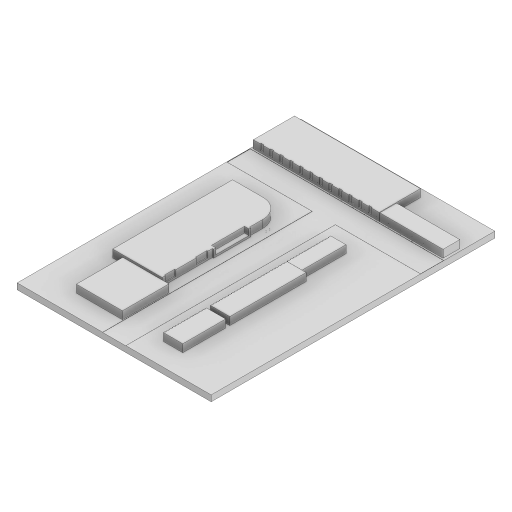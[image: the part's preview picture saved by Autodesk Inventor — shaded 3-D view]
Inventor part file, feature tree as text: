
AUTODESK INVENTOR PART (.ipt)
format: ipt  version: 2023 (Build 270158000, 158)  size: 555,008 bytes
history: native  units: in
note: dims shown in document units (in); Inventor stores cm internally (conversion verified against a paired STEP export)
features: projected_geometry x16, extrude x10, sketch x10, pattern_linear x3
ambient origin geometry x8: Origin, YZ Plane, XZ Plane, XY Plane, X Axis, Y Axis, Z Axis, Center Point
bodies: Solid1 (feature_tree)
feature tree (39):
  extrude  "Extrusion1"  Depth=472.4409in
  extrude  "Extrusion2"  Depth=3937.0079in
  extrude  "Extrusion3"  Depth=4.0in TaperAngle=0.0deg
  extrude  "Extrusion4"  Depth=157.4803in TaperAngle=0.0deg
  extrude  "Extrusion5"  Depth=118.1102in TaperAngle=0.0deg
  extrude  "Extrusion6"  Depth=118.1102in TaperAngle=0.0deg
  extrude  "Extrusion7"  Depth=39.3701in
  extrude  "Extrusion8"  Depth=78.7402in
  pattern_linear  "Rectangular Pattern1"  Count1=200 Spacing1=0.0in
  extrude  "Extrusion9"  Depth=118.1102in TaperAngle=0.0deg
  pattern_linear  "Rectangular Pattern2"  Count1=10 Spacing1=360.0in
  extrude  "Extrusion10"  Depth=60.0in
  pattern_linear  "Rectangular Pattern3"  [2 undecoded]
  sketch  "Sketch1"  dims[d0=1968.5039in d1=472.4409in]
  sketch  "Sketch2"  dims[d2=472.4409in d3=3937.0079in]
  projected_geometry  "Projected Loop1"
  sketch  "Sketch3"  dims[d4=1.0in d5=0.0in d6=4.0in d7=0.0in]
  projected_geometry  "Projected Loop2"
  sketch  "Sketch4"  dims[d8=393.7008in d9=157.4803in d10=0.0in]
  projected_geometry  "Projected Loop3"
  projected_geometry  "Projected Loop4"
  projected_geometry  "Projected Loop5"
  projected_geometry  "Projected Loop6"
  projected_geometry  "Projected Loop7"
  projected_geometry  "Projected Loop8"
  projected_geometry  "Projected Loop9"
  sketch  "Sketch5"  dims[d11=4.7244in d13=200.0in d14=0.3937in d16=1.0in d18=118.1102in d19=0.0in]
  projected_geometry  "Projected Loop10"
  sketch  "Sketch6"  dims[d20=118.1102in d21=0.0in d22=118.1102in d23=0.0in]
  projected_geometry  "Projected Loop11"
  projected_geometry  "Projected Loop12"
  sketch  "Sketch7"  dims[d24=39.3701in d25=0.0in d26=5.0in]
  projected_geometry  "Projected Loop13"
  sketch  "Sketch8"  dims[d27=5.0in d28=6.0in d29=78.7402in d30=0.0in]
  projected_geometry  "Projected Loop14"
  sketch  "Sketch9"  dims[d31=3.937in d33=240.0in d34=118.1102in d35=0.0in d36=3.937in d38=360.0in]
  sketch  "Sketch10"  dims[d39=118.1102in d40=0.0in d41=22.0472in d43=60.0in]
  projected_geometry  "Projected Loop15"
  projected_geometry  "Projected Loop16"
note: 2 required parameter values undecoded (feature->parameter linkage not recoverable at this tier; creation-order binding heuristic only, values carry confidence <= 0.55)
